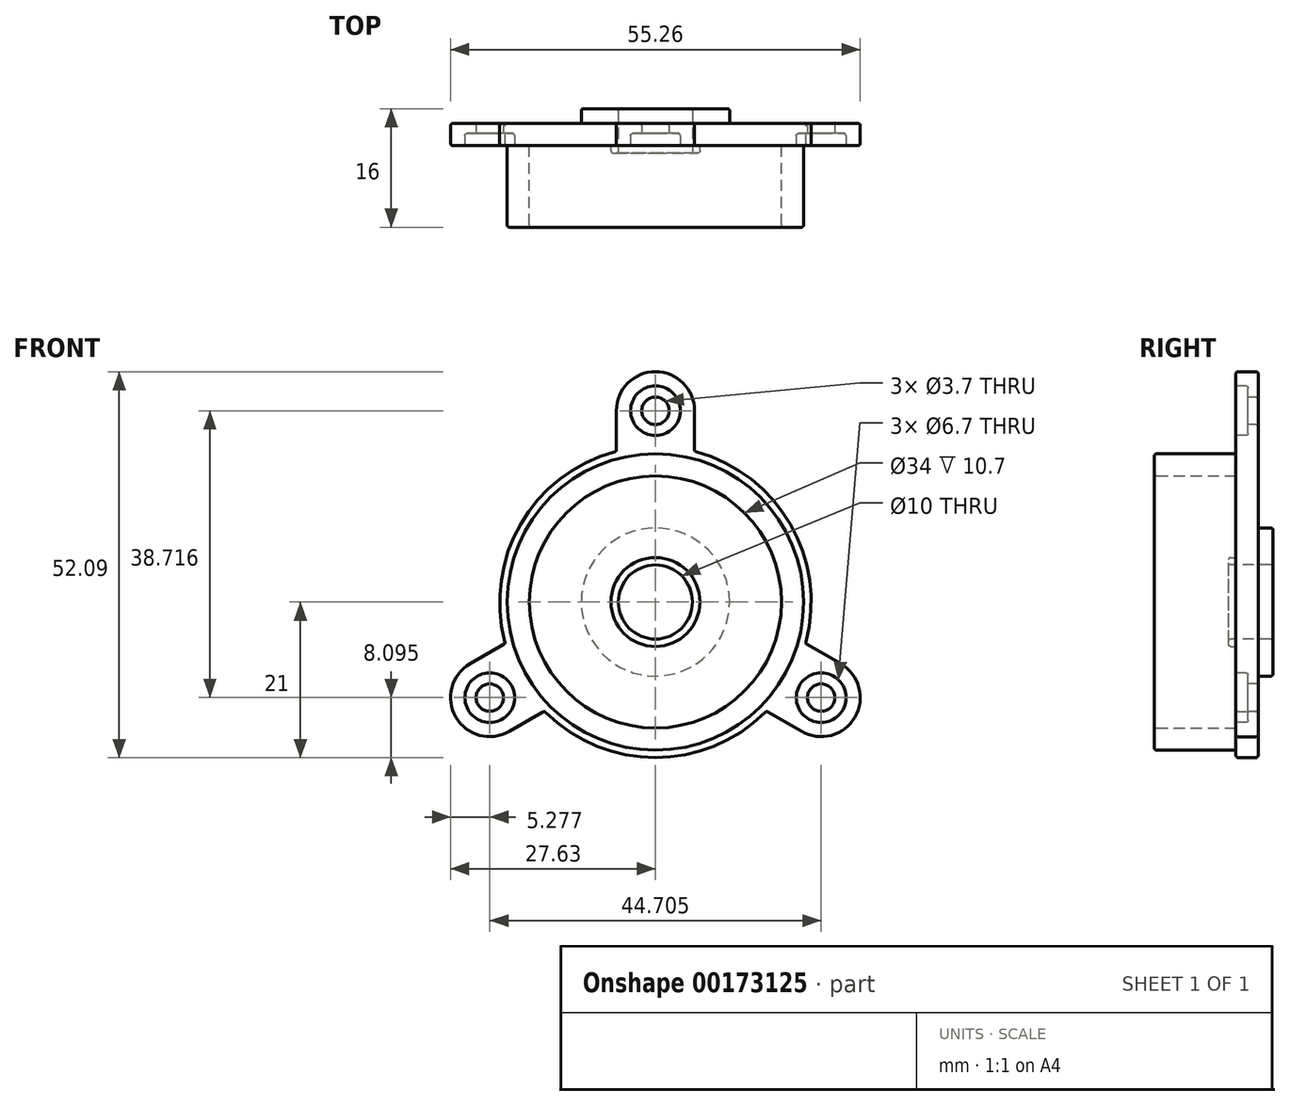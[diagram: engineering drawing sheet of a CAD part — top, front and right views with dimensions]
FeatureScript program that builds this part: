
annotation { "Feature Type Name" : "Feature", "Feature Type Description" : "" }
export const myFeature = defineFeature(function(context is Context, id is Id, definition is map)
    precondition{}
    {
        {
            var Q0;
            Q0=qCreatedBy(makeId("Front.planeOp"),FACE);
            var sketch = newSketch(context, id + "F0", { "sketchPlane" : qUnion([Q0])});
            skArc(sketch, "E0", {"start": v(-5.28, 20.33) * mm, "mid": v(-18.19, 10.5) * mm, "end": v(-20.24, -5.6) * mm});
            skLineSegment(sketch, "E1", {"start": v(-5.28, 25.81) * mm, "end": v(-5.28, 20.33) * mm});
            skLineSegment(sketch, "E2", {"start": v(5.28, 25.81) * mm, "end": v(5.28, 20.33) * mm});
            skArc(sketch, "E3.trimOffspring", {"start": v(5.28, 25.81) * mm, "mid": v(0, 31.09) * mm, "end": v(-5.28, 25.81) * mm});
            skLineSegment(sketch, "E4.1.0", {"start": v(-25, -8.34) * mm, "end": v(-20.24, -5.6) * mm});
            skArc(sketch, "E4.1.1", {"start": v(-25, -8.34) * mm, "mid": v(-26.92, -15.54) * mm, "end": v(-19.71, -17.47) * mm});
            skLineSegment(sketch, "E4.1.2", {"start": v(-19.71, -17.47) * mm, "end": v(-14.97, -14.73) * mm});
            skLineSegment(sketch, "E4.2.0", {"start": v(19.71, -17.47) * mm, "end": v(14.97, -14.73) * mm});
            skArc(sketch, "E4.2.1", {"start": v(19.71, -17.47) * mm, "mid": v(26.92, -15.54) * mm, "end": v(25, -8.34) * mm});
            skLineSegment(sketch, "E4.2.2", {"start": v(25, -8.34) * mm, "end": v(20.24, -5.6) * mm});
            skArc(sketch, "E5.trimOffspring", {"start": v(-14.97, -14.73) * mm, "mid": v(0, -21) * mm, "end": v(14.97, -14.73) * mm});
            skArc(sketch, "E6.trimOffspring", {"start": v(20.24, -5.6) * mm, "mid": v(18.19, 10.5) * mm, "end": v(5.28, 20.33) * mm});
            skSolve(sketch);
        }
        {
            var Q0;
            Q0=makeQuery(id+"F0.imprint","IMPRINT",FACE,{"disambiguationData":[TD([[makeQuery(id+"F0.imprint","IMPRINT",EDGE,{"derivedFrom":sQuery(id+"F0.wireOp",EDGE,"E0")}),1.0]])]});
            extrude(context, id + "F1", {"entities" : qUnion([Q0]), "depth" : 3 * mm});
        }
        {
            var Q0;
            Q0=makeQuery(id+"F1.opExtrude","CAP_FACE",FACE,{"disambiguationData":[OSD([sQuery(id+"F0.wireOp",EDGE,"E0"),sQuery(id+"F0.wireOp",EDGE,"E1"),sQuery(id+"F0.wireOp",EDGE,"E2"),sQuery(id+"F0.wireOp",EDGE,"E3.trimOffspring"),sQuery(id+"F0.wireOp",EDGE,"E4.1.0"),sQuery(id+"F0.wireOp",EDGE,"E4.1.1"),sQuery(id+"F0.wireOp",EDGE,"E4.1.2"),sQuery(id+"F0.wireOp",EDGE,"E4.2.0"),sQuery(id+"F0.wireOp",EDGE,"E4.2.1"),sQuery(id+"F0.wireOp",EDGE,"E4.2.2"),sQuery(id+"F0.wireOp",EDGE,"E5.trimOffspring"),sQuery(id+"F0.wireOp",EDGE,"E6.trimOffspring")])],"isStart":false});
            var sketch = newSketch(context, id + "F2", { "sketchPlane" : qUnion([Q0])});
            skCircle(sketch, "E7", {"center": v(0, 25.81) * mm, "radius": 1.85 * mm});
            skCircle(sketch, "E8.1.0", {"center": v(-22.35, -12.9) * mm, "radius": 1.85 * mm});
            skCircle(sketch, "E8.2.0", {"center": v(22.35, -12.9) * mm, "radius": 1.85 * mm});
            skPoint(sketch, "E8.center", {"position": v(0, 0) * mm});
            skSolve(sketch);
        }
        {
            var Q0;
            Q0=makeQuery(id+"F2.imprint","IMPRINT",FACE,{"disambiguationData":[TD([[makeQuery(id+"F2.imprint","IMPRINT",EDGE,{"derivedFrom":sQuery(id+"F2.wireOp",EDGE,"E7")}),1.0]])]});
            var Q1;
            Q1=makeQuery(id+"F2.imprint","IMPRINT",FACE,{"disambiguationData":[TD([[makeQuery(id+"F2.imprint","IMPRINT",EDGE,{"derivedFrom":sQuery(id+"F2.wireOp",EDGE,"E8.1.0")}),1.0]])]});
            var Q2;
            Q2=makeQuery(id+"F2.imprint","IMPRINT",FACE,{"disambiguationData":[TD([[makeQuery(id+"F2.imprint","IMPRINT",EDGE,{"derivedFrom":sQuery(id+"F2.wireOp",EDGE,"E8.2.0")}),1.0]])]});
            extrude(context, id + "F3", {"entities" : qUnion([Q0, Q1, Q2]), "operationType" : NewBodyOperationType.REMOVE, "endBound" : BoundingType.THROUGH_ALL, "oppositeDirection" : true, "depth" : 25 * mm});
        }
        {
            var Q0;
            Q0=makeQuery(id+"F1.opExtrude","CAP_FACE",FACE,{"disambiguationData":[OSD([sQuery(id+"F0.wireOp",EDGE,"E0"),sQuery(id+"F0.wireOp",EDGE,"E1"),sQuery(id+"F0.wireOp",EDGE,"E2"),sQuery(id+"F0.wireOp",EDGE,"E3.trimOffspring"),sQuery(id+"F0.wireOp",EDGE,"E4.1.0"),sQuery(id+"F0.wireOp",EDGE,"E4.1.1"),sQuery(id+"F0.wireOp",EDGE,"E4.1.2"),sQuery(id+"F0.wireOp",EDGE,"E4.2.0"),sQuery(id+"F0.wireOp",EDGE,"E4.2.1"),sQuery(id+"F0.wireOp",EDGE,"E4.2.2"),sQuery(id+"F0.wireOp",EDGE,"E5.trimOffspring"),sQuery(id+"F0.wireOp",EDGE,"E6.trimOffspring")])],"isStart":false});
            var sketch = newSketch(context, id + "F4", { "sketchPlane" : qUnion([Q0])});
            skCircle(sketch, "E9", {"center": v(0, 0) * mm, "radius": 17 * mm});
            skCircle(sketch, "E10", {"center": v(0, 0) * mm, "radius": 20 * mm});
            skSolve(sketch);
        }
        {
            var Q0;
            Q0=makeQuery(id+"F4.imprint","IMPRINT",FACE,{"disambiguationData":[TD([[makeQuery(id+"F4.imprint","IMPRINT",EDGE,{"derivedFrom":sQuery(id+"F4.wireOp",EDGE,"E9")}),-1.0]])]});
            extrude(context, id + "F5", {"entities" : qUnion([Q0]), "operationType" : NewBodyOperationType.ADD, "depth" : 11 * mm});
        }
        {
            var Q0;
            {var subQ0=sQuery(id+"F0.wireOp",EDGE,"E4.2.2");var subQ1=sQuery(id+"F0.wireOp",EDGE,"E4.2.0");var subQ2=sQuery(id+"F0.wireOp",EDGE,"E4.1.2");var subQ3=sQuery(id+"F0.wireOp",EDGE,"E4.1.1");var subQ4=sQuery(id+"F0.wireOp",EDGE,"E4.1.0");var subQ5=sQuery(id+"F0.wireOp",EDGE,"E0");var subQ6=sQuery(id+"F0.wireOp",EDGE,"E4.2.1");var subQ7=sQuery(id+"F0.wireOp",EDGE,"E1");var subQ8=sQuery(id+"F0.wireOp",EDGE,"E2");var subQ9=sQuery(id+"F0.wireOp",EDGE,"E3.trimOffspring");var subQ10=sQuery(id+"F0.wireOp",EDGE,"E5.trimOffspring");var subQ11=sQuery(id+"F0.wireOp",EDGE,"E6.trimOffspring");Q0=makeQuery(id+"F5.boolean.opBoolean","SPLIT",FACE,{"disambiguationData":[TD([makeQuery(id+"F1.opExtrude","SWEPT_FACE",FACE,{"disambiguationData":[OSD([subQ5])]})])],"derivedFrom":makeQuery(id+"F1.opExtrude","CAP_FACE",FACE,{"disambiguationData":[OSD([subQ5,subQ7,subQ8,subQ9,subQ4,subQ3,subQ2,subQ1,subQ6,subQ0,subQ10,subQ11])],"isStart":false})});}
            var sketch = newSketch(context, id + "F6", { "sketchPlane" : qUnion([Q0])});
            skCircle(sketch, "E11", {"center": v(-22.35, -12.9) * mm, "radius": 3.35 * mm});
            skCircle(sketch, "E12.1.0", {"center": v(22.35, -12.9) * mm, "radius": 3.35 * mm});
            skCircle(sketch, "E12.2.0", {"center": v(0, 25.81) * mm, "radius": 3.35 * mm});
            skPoint(sketch, "E12.center", {"position": v(0, 0) * mm});
            skSolve(sketch);
        }
        {
            var Q0;
            Q0=makeQuery(id+"F6.imprint","IMPRINT",FACE,{"disambiguationData":[TD([[makeQuery(id+"F6.imprint","IMPRINT",EDGE,{"derivedFrom":sQuery(id+"F6.wireOp",EDGE,"E11")}),1.0]])]});
            var Q1;
            Q1=makeQuery(id+"F6.imprint","IMPRINT",FACE,{"disambiguationData":[TD([[makeQuery(id+"F6.imprint","IMPRINT",EDGE,{"derivedFrom":sQuery(id+"F6.wireOp",EDGE,"E12.1.0")}),1.0]])]});
            var Q2;
            Q2=makeQuery(id+"F6.imprint","IMPRINT",FACE,{"disambiguationData":[TD([[makeQuery(id+"F6.imprint","IMPRINT",EDGE,{"derivedFrom":sQuery(id+"F6.wireOp",EDGE,"E12.2.0")}),1.0]])]});
            extrude(context, id + "F7", {"entities" : qUnion([Q0, Q1, Q2]), "operationType" : NewBodyOperationType.REMOVE, "oppositeDirection" : true, "depth" : 1.65 * mm});
        }
        {
            var Q0;
            Q0=makeQuery(id+"F5.boolean.opBoolean","SPLIT",FACE,{"disambiguationData":[TD([makeQuery(id+"F5.opExtrude","SWEPT_FACE",FACE,{"disambiguationData":[OSD([sQuery(id+"F4.wireOp",EDGE,"E9")])]})])],"derivedFrom":makeQuery(id+"F1.opExtrude","CAP_FACE",FACE,{"disambiguationData":[OSD([sQuery(id+"F0.wireOp",EDGE,"E0"),sQuery(id+"F0.wireOp",EDGE,"E1"),sQuery(id+"F0.wireOp",EDGE,"E2"),sQuery(id+"F0.wireOp",EDGE,"E3.trimOffspring"),sQuery(id+"F0.wireOp",EDGE,"E4.1.0"),sQuery(id+"F0.wireOp",EDGE,"E4.1.1"),sQuery(id+"F0.wireOp",EDGE,"E4.1.2"),sQuery(id+"F0.wireOp",EDGE,"E4.2.0"),sQuery(id+"F0.wireOp",EDGE,"E4.2.1"),sQuery(id+"F0.wireOp",EDGE,"E4.2.2"),sQuery(id+"F0.wireOp",EDGE,"E5.trimOffspring"),sQuery(id+"F0.wireOp",EDGE,"E6.trimOffspring")])],"isStart":false})});
            var sketch = newSketch(context, id + "F8", { "sketchPlane" : qUnion([Q0])});
            skCircle(sketch, "E13", {"center": v(0, 0) * mm, "radius": 5 * mm});
            skSolve(sketch);
        }
        {
            var Q0;
            Q0=makeQuery(id+"F8.imprint","IMPRINT",FACE,{"disambiguationData":[TD([[makeQuery(id+"F8.imprint","IMPRINT",EDGE,{"derivedFrom":sQuery(id+"F8.wireOp",EDGE,"E13")}),1.0]])]});
            extrude(context, id + "F9", {"entities" : qUnion([Q0]), "operationType" : NewBodyOperationType.REMOVE, "endBound" : BoundingType.THROUGH_ALL, "oppositeDirection" : true, "depth" : 25 * mm});
        }
        {
            var Q0;
            Q0=makeQuery(id+"F5.boolean.opBoolean","SPLIT",FACE,{"disambiguationData":[TD([makeQuery(id+"F5.opExtrude","SWEPT_FACE",FACE,{"disambiguationData":[OSD([sQuery(id+"F4.wireOp",EDGE,"E9")])]})])],"derivedFrom":makeQuery(id+"F1.opExtrude","CAP_FACE",FACE,{"disambiguationData":[OSD([sQuery(id+"F0.wireOp",EDGE,"E0"),sQuery(id+"F0.wireOp",EDGE,"E1"),sQuery(id+"F0.wireOp",EDGE,"E2"),sQuery(id+"F0.wireOp",EDGE,"E3.trimOffspring"),sQuery(id+"F0.wireOp",EDGE,"E4.1.0"),sQuery(id+"F0.wireOp",EDGE,"E4.1.1"),sQuery(id+"F0.wireOp",EDGE,"E4.1.2"),sQuery(id+"F0.wireOp",EDGE,"E4.2.0"),sQuery(id+"F0.wireOp",EDGE,"E4.2.1"),sQuery(id+"F0.wireOp",EDGE,"E4.2.2"),sQuery(id+"F0.wireOp",EDGE,"E5.trimOffspring"),sQuery(id+"F0.wireOp",EDGE,"E6.trimOffspring")])],"isStart":false})});
            var sketch = newSketch(context, id + "F10", { "sketchPlane" : qUnion([Q0])});
            skCircle(sketch, "E14", {"center": v(0, 0) * mm, "radius": 6 * mm});
            skSolve(sketch);
        }
        {
            var Q0;
            Q0=makeQuery(id+"F10.imprint","IMPRINT",FACE,{"disambiguationData":[TD([[makeQuery(id+"F10.imprint","IMPRINT",EDGE,{"derivedFrom":sQuery(id+"F10.wireOp",EDGE,"E14")}),1.0]])]});
            extrude(context, id + "F11", {"entities" : qUnion([Q0]), "operationType" : NewBodyOperationType.ADD, "depth" : 1 * mm});
        }
        {
            var Q0;
            Q0=makeQuery(id+"F1.opExtrude","CAP_FACE",FACE,{"disambiguationData":[OSD([sQuery(id+"F0.wireOp",EDGE,"E0"),sQuery(id+"F0.wireOp",EDGE,"E1"),sQuery(id+"F0.wireOp",EDGE,"E2"),sQuery(id+"F0.wireOp",EDGE,"E3.trimOffspring"),sQuery(id+"F0.wireOp",EDGE,"E4.1.0"),sQuery(id+"F0.wireOp",EDGE,"E4.1.1"),sQuery(id+"F0.wireOp",EDGE,"E4.1.2"),sQuery(id+"F0.wireOp",EDGE,"E4.2.0"),sQuery(id+"F0.wireOp",EDGE,"E4.2.1"),sQuery(id+"F0.wireOp",EDGE,"E4.2.2"),sQuery(id+"F0.wireOp",EDGE,"E5.trimOffspring"),sQuery(id+"F0.wireOp",EDGE,"E6.trimOffspring")])],"isStart":true});
            var sketch = newSketch(context, id + "F12", { "sketchPlane" : qUnion([Q0])});
            skCircle(sketch, "E15", {"center": v(0, 0) * mm, "radius": 10 * mm});
            skSolve(sketch);
        }
        {
            var Q0;
            Q0=makeQuery(id+"F12.imprint","IMPRINT",FACE,{"disambiguationData":[TD([[makeQuery(id+"F12.imprint","IMPRINT",EDGE,{"derivedFrom":sQuery(id+"F12.wireOp",EDGE,"E15")}),1.0]])]});
            extrude(context, id + "F13", {"entities" : qUnion([Q0]), "operationType" : NewBodyOperationType.ADD, "depth" : 2 * mm});
        }
        {
            var Q0;
            Q0=makeQuery(id+"F5.opExtrude","CAP_EDGE",EDGE,{"disambiguationData":[OSD([sQuery(id+"F4.wireOp",EDGE,"E10")])],"isStart":false});
            var Q1;
            Q1=makeQuery(id+"F5.opExtrude","CAP_EDGE",EDGE,{"disambiguationData":[OSD([sQuery(id+"F4.wireOp",EDGE,"E9")])],"isStart":false});
            var Q2;
            Q2=makeQuery(id+"F11.opExtrude","CAP_EDGE",EDGE,{"disambiguationData":[OSD([sQuery(id+"F10.wireOp",EDGE,"E14")])],"isStart":false});
            var Q3;
            Q3=makeQuery(id+"F11.opExtrude","CAP_EDGE",EDGE,{"disambiguationData":[OSD([sQuery(id+"F8.wireOp",EDGE,"E13")])],"isStart":false});
            var Q4;
            Q4=makeQuery(id+"F11.opExtrude","CAP_EDGE",EDGE,{"disambiguationData":[OSD([sQuery(id+"F10.wireOp",EDGE,"E14")])],"isStart":true});
            var Q5;
            Q5=makeQuery(id+"F5.opExtrude","CAP_EDGE",EDGE,{"disambiguationData":[OSD([sQuery(id+"F4.wireOp",EDGE,"E9")])],"isStart":true});
            var Q6;
            Q6=makeQuery(id+"F7.boolean.opBoolean","COPY",EDGE,{"derivedFrom":makeQuery(id+"F7.opExtrude","CAP_EDGE",EDGE,{"disambiguationData":[OSD([sQuery(id+"F6.wireOp",EDGE,"E11")])],"isStart":true})});
            var Q7;
            Q7=makeQuery(id+"F7.boolean.opBoolean","COPY",EDGE,{"derivedFrom":makeQuery(id+"F7.opExtrude","CAP_EDGE",EDGE,{"disambiguationData":[OSD([sQuery(id+"F2.wireOp",EDGE,"E8.1.0")])],"isStart":false})});
            var Q8;
            Q8=makeQuery(id+"F1.opExtrude","CAP_EDGE",EDGE,{"disambiguationData":[OSD([sQuery(id+"F0.wireOp",EDGE,"E4.1.1")])],"isStart":false});
            var Q9;
            Q9=makeQuery(id+"F1.opExtrude","CAP_EDGE",EDGE,{"disambiguationData":[OSD([sQuery(id+"F0.wireOp",EDGE,"E4.1.1")])],"isStart":true});
            var Q10;
            Q10=makeQuery(id+"F1.opExtrude","CAP_EDGE",EDGE,{"disambiguationData":[OSD([sQuery(id+"F0.wireOp",EDGE,"E4.1.2")])],"isStart":false});
            var Q11;
            Q11=makeQuery(id+"F1.opExtrude","CAP_EDGE",EDGE,{"disambiguationData":[OSD([sQuery(id+"F0.wireOp",EDGE,"E4.1.0")])],"isStart":false});
            var Q12;
            Q12=makeQuery(id+"F1.opExtrude","CAP_EDGE",EDGE,{"disambiguationData":[OSD([sQuery(id+"F0.wireOp",EDGE,"E0")])],"isStart":false});
            var Q13;
            Q13=makeQuery(id+"F5.opExtrude","CAP_EDGE",EDGE,{"disambiguationData":[OSD([sQuery(id+"F4.wireOp",EDGE,"E10")])],"isStart":true});
            var Q14;
            Q14=makeQuery(id+"F1.opExtrude","CAP_EDGE",EDGE,{"disambiguationData":[OSD([sQuery(id+"F0.wireOp",EDGE,"E5.trimOffspring")])],"isStart":false});
            var Q15;
            Q15=makeQuery(id+"F1.opExtrude","CAP_EDGE",EDGE,{"disambiguationData":[OSD([sQuery(id+"F0.wireOp",EDGE,"E4.2.0")])],"isStart":false});
            var Q16;
            Q16=makeQuery(id+"F1.opExtrude","CAP_EDGE",EDGE,{"disambiguationData":[OSD([sQuery(id+"F0.wireOp",EDGE,"E5.trimOffspring")])],"isStart":true});
            var Q17;
            Q17=makeQuery(id+"F1.opExtrude","CAP_EDGE",EDGE,{"disambiguationData":[OSD([sQuery(id+"F0.wireOp",EDGE,"E4.2.1")])],"isStart":false});
            var Q18;
            Q18=makeQuery(id+"F1.opExtrude","CAP_EDGE",EDGE,{"disambiguationData":[OSD([sQuery(id+"F0.wireOp",EDGE,"E4.2.2")])],"isStart":false});
            var Q19;
            Q19=makeQuery(id+"F1.opExtrude","CAP_EDGE",EDGE,{"disambiguationData":[OSD([sQuery(id+"F0.wireOp",EDGE,"E6.trimOffspring")])],"isStart":false});
            var Q20;
            Q20=makeQuery(id+"F1.opExtrude","CAP_EDGE",EDGE,{"disambiguationData":[OSD([sQuery(id+"F0.wireOp",EDGE,"E6.trimOffspring")])],"isStart":true});
            var Q21;
            Q21=makeQuery(id+"F7.boolean.opBoolean","COPY",EDGE,{"derivedFrom":makeQuery(id+"F7.opExtrude","CAP_EDGE",EDGE,{"disambiguationData":[OSD([sQuery(id+"F6.wireOp",EDGE,"E12.1.0")])],"isStart":true})});
            var Q22;
            Q22=makeQuery(id+"F7.boolean.opBoolean","COPY",EDGE,{"derivedFrom":makeQuery(id+"F7.opExtrude","CAP_EDGE",EDGE,{"disambiguationData":[OSD([sQuery(id+"F6.wireOp",EDGE,"E12.1.0")])],"isStart":false})});
            var Q23;
            Q23=makeQuery(id+"F7.boolean.opBoolean","COPY",EDGE,{"derivedFrom":makeQuery(id+"F7.opExtrude","CAP_EDGE",EDGE,{"disambiguationData":[OSD([sQuery(id+"F6.wireOp",EDGE,"E11")])],"isStart":false})});
            var Q24;
            Q24=makeQuery(id+"F7.boolean.opBoolean","COPY",EDGE,{"derivedFrom":makeQuery(id+"F7.opExtrude","CAP_EDGE",EDGE,{"disambiguationData":[OSD([sQuery(id+"F2.wireOp",EDGE,"E8.2.0")])],"isStart":false})});
            var Q25;
            Q25=makeQuery(id+"F1.opExtrude","CAP_EDGE",EDGE,{"disambiguationData":[OSD([sQuery(id+"F0.wireOp",EDGE,"E4.1.2")])],"isStart":true});
            var Q26;
            Q26=makeQuery(id+"F1.opExtrude","SWEPT_EDGE",EDGE,{"disambiguationData":[OSD([sQuery(id+"F0.wireOp",EDGE,"E4.1.2"),sQuery(id+"F0.wireOp",EDGE,"E5.trimOffspring")])]});
            var Q27;
            Q27=makeQuery(id+"F1.opExtrude","SWEPT_EDGE",EDGE,{"disambiguationData":[OSD([sQuery(id+"F0.wireOp",EDGE,"E4.2.0"),sQuery(id+"F0.wireOp",EDGE,"E5.trimOffspring")])]});
            var Q28;
            Q28=makeQuery(id+"F1.opExtrude","CAP_EDGE",EDGE,{"disambiguationData":[OSD([sQuery(id+"F0.wireOp",EDGE,"E4.2.0")])],"isStart":true});
            var Q29;
            Q29=makeQuery(id+"F1.opExtrude","CAP_EDGE",EDGE,{"disambiguationData":[OSD([sQuery(id+"F0.wireOp",EDGE,"E4.2.1")])],"isStart":true});
            var Q30;
            Q30=makeQuery(id+"F13.opExtrude","CAP_EDGE",EDGE,{"disambiguationData":[OSD([sQuery(id+"F0.wireOp",EDGE,"E0"),sQuery(id+"F0.wireOp",EDGE,"E1"),sQuery(id+"F0.wireOp",EDGE,"E2"),sQuery(id+"F0.wireOp",EDGE,"E3.trimOffspring"),sQuery(id+"F0.wireOp",EDGE,"E4.1.0"),sQuery(id+"F0.wireOp",EDGE,"E4.1.1"),sQuery(id+"F0.wireOp",EDGE,"E4.1.2"),sQuery(id+"F0.wireOp",EDGE,"E4.2.0"),sQuery(id+"F0.wireOp",EDGE,"E4.2.1"),sQuery(id+"F0.wireOp",EDGE,"E4.2.2"),sQuery(id+"F0.wireOp",EDGE,"E5.trimOffspring"),sQuery(id+"F0.wireOp",EDGE,"E6.trimOffspring"),sQuery(id+"F8.wireOp",EDGE,"E13")])],"isStart":false});
            var Q31;
            Q31=makeQuery(id+"F1.opExtrude","CAP_EDGE",EDGE,{"disambiguationData":[OSD([sQuery(id+"F0.wireOp",EDGE,"E2")])],"isStart":false});
            var Q32;
            Q32=makeQuery(id+"F1.opExtrude","CAP_EDGE",EDGE,{"disambiguationData":[OSD([sQuery(id+"F0.wireOp",EDGE,"E1")])],"isStart":false});
            var Q33;
            Q33=makeQuery(id+"F1.opExtrude","CAP_EDGE",EDGE,{"disambiguationData":[OSD([sQuery(id+"F0.wireOp",EDGE,"E3.trimOffspring")])],"isStart":false});
            var Q34;
            Q34=makeQuery(id+"F7.boolean.opBoolean","COPY",EDGE,{"derivedFrom":makeQuery(id+"F7.opExtrude","CAP_EDGE",EDGE,{"disambiguationData":[OSD([sQuery(id+"F6.wireOp",EDGE,"E12.2.0")])],"isStart":true})});
            var Q35;
            Q35=makeQuery(id+"F7.boolean.opBoolean","COPY",EDGE,{"derivedFrom":makeQuery(id+"F7.opExtrude","CAP_EDGE",EDGE,{"disambiguationData":[OSD([sQuery(id+"F6.wireOp",EDGE,"E12.2.0")])],"isStart":false})});
            var Q36;
            Q36=makeQuery(id+"F7.boolean.opBoolean","COPY",EDGE,{"derivedFrom":makeQuery(id+"F7.opExtrude","CAP_EDGE",EDGE,{"disambiguationData":[OSD([sQuery(id+"F2.wireOp",EDGE,"E7")])],"isStart":false})});
            var Q37;
            Q37=makeQuery(id+"F3.boolean.opBoolean","INTERSECT",EDGE,{"derivedFrom":[makeQuery(id+"F1.opExtrude","CAP_FACE",FACE,{"disambiguationData":[OSD([sQuery(id+"F0.wireOp",EDGE,"E0"),sQuery(id+"F0.wireOp",EDGE,"E1"),sQuery(id+"F0.wireOp",EDGE,"E2"),sQuery(id+"F0.wireOp",EDGE,"E3.trimOffspring"),sQuery(id+"F0.wireOp",EDGE,"E4.1.0"),sQuery(id+"F0.wireOp",EDGE,"E4.1.1"),sQuery(id+"F0.wireOp",EDGE,"E4.1.2"),sQuery(id+"F0.wireOp",EDGE,"E4.2.0"),sQuery(id+"F0.wireOp",EDGE,"E4.2.1"),sQuery(id+"F0.wireOp",EDGE,"E4.2.2"),sQuery(id+"F0.wireOp",EDGE,"E5.trimOffspring"),sQuery(id+"F0.wireOp",EDGE,"E6.trimOffspring")])],"isStart":true}),makeQuery(id+"F3.opExtrude","SWEPT_FACE",FACE,{"disambiguationData":[OSD([sQuery(id+"F2.wireOp",EDGE,"E7")])]})]});
            var Q38;
            Q38=makeQuery(id+"F1.opExtrude","CAP_EDGE",EDGE,{"disambiguationData":[OSD([sQuery(id+"F0.wireOp",EDGE,"E2")])],"isStart":true});
            var Q39;
            Q39=makeQuery(id+"F1.opExtrude","CAP_EDGE",EDGE,{"disambiguationData":[OSD([sQuery(id+"F0.wireOp",EDGE,"E3.trimOffspring")])],"isStart":true});
            var Q40;
            Q40=makeQuery(id+"F1.opExtrude","CAP_EDGE",EDGE,{"disambiguationData":[OSD([sQuery(id+"F0.wireOp",EDGE,"E1")])],"isStart":true});
            var Q41;
            Q41=makeQuery(id+"F1.opExtrude","SWEPT_EDGE",EDGE,{"disambiguationData":[OSD([sQuery(id+"F0.wireOp",EDGE,"E0"),sQuery(id+"F0.wireOp",EDGE,"E1")])]});
            var Q42;
            Q42=makeQuery(id+"F1.opExtrude","CAP_EDGE",EDGE,{"disambiguationData":[OSD([sQuery(id+"F0.wireOp",EDGE,"E0")])],"isStart":true});
            var Q43;
            Q43=makeQuery(id+"F13.opExtrude","CAP_EDGE",EDGE,{"disambiguationData":[OSD([sQuery(id+"F12.wireOp",EDGE,"E15")])],"isStart":false});
            var Q44;
            Q44=makeQuery(id+"F13.opExtrude","CAP_EDGE",EDGE,{"disambiguationData":[OSD([sQuery(id+"F12.wireOp",EDGE,"E15")])],"isStart":true});
            var Q45;
            Q45=makeQuery(id+"F1.opExtrude","SWEPT_EDGE",EDGE,{"disambiguationData":[OSD([sQuery(id+"F0.wireOp",EDGE,"E4.2.2"),sQuery(id+"F0.wireOp",EDGE,"E6.trimOffspring")])]});
            var Q46;
            Q46=makeQuery(id+"F1.opExtrude","SWEPT_EDGE",EDGE,{"disambiguationData":[OSD([sQuery(id+"F0.wireOp",EDGE,"E2"),sQuery(id+"F0.wireOp",EDGE,"E6.trimOffspring")])]});
            var Q47;
            Q47=makeQuery(id+"F1.opExtrude","CAP_EDGE",EDGE,{"disambiguationData":[OSD([sQuery(id+"F0.wireOp",EDGE,"E4.2.2")])],"isStart":true});
            var Q48;
            Q48=makeQuery(id+"F1.opExtrude","SWEPT_EDGE",EDGE,{"disambiguationData":[OSD([sQuery(id+"F0.wireOp",EDGE,"E0"),sQuery(id+"F0.wireOp",EDGE,"E4.1.0")])]});
            var Q49;
            Q49=makeQuery(id+"F1.opExtrude","CAP_EDGE",EDGE,{"disambiguationData":[OSD([sQuery(id+"F0.wireOp",EDGE,"E4.1.0")])],"isStart":true});
            fillet(context, id + "F14", {"entities" : qUnion([Q0, Q1, Q2, Q3, Q4, Q5, Q6, Q7, Q8, Q9, Q10, Q11, Q12, Q13, Q14, Q15, Q16, Q17, Q18, Q19, Q20, Q21, Q22, Q23, Q24, Q25, Q26, Q27, Q28, Q29, Q30, Q31, Q32, Q33, Q34, Q35, Q36, Q37, Q38, Q39, Q40, Q41, Q42, Q43, Q44, Q45, Q46, Q47, Q48, Q49]), "radius" : .3 * mm, "tangentPropagation" : true, "allowEdgeOverflow" : false});
        }
    });
